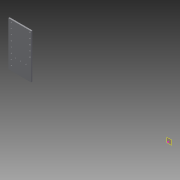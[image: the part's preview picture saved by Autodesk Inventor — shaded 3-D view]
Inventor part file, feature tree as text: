
AUTODESK INVENTOR PART (.ipt)
format: ipt  version: 2015 (Build 190159000, 159)  size: 106,496 bytes
history: native  units: in
note: dims shown in document units (in); Inventor stores cm internally (conversion verified against a paired STEP export)
features: sketch x4, reference x4, extrude x3, plane x1
ambient origin geometry x8: Origin, YZ Plane, XZ Plane, XY Plane, X Axis, Y Axis, Z Axis, Center Point
bodies: Solid1 (feature_tree)
feature tree (12):
  plane  "Work Plane3"
  extrude  "Extrusion1"  Depth=0.25in TaperAngle=0.0deg
  sketch  "Sketch3"  dims[d4=0.25in d5=0.0in]
  extrude  "Extrusion2"  [1 undecoded]
  extrude  "Extrusion3"  [1 undecoded]
  sketch  "Sketch1"  dims[d0=0.25in d1=0.0in d2=0.25in d3=0.0in]
  sketch  "Sketch4"
  reference  "Reference27"
  reference  "Reference28"
  sketch  "Sketch5"
  reference  "Reference29"
  reference  "Reference30"
note: 2 required parameter values undecoded (feature->parameter linkage not recoverable at this tier; creation-order binding heuristic only, values carry confidence <= 0.55)
